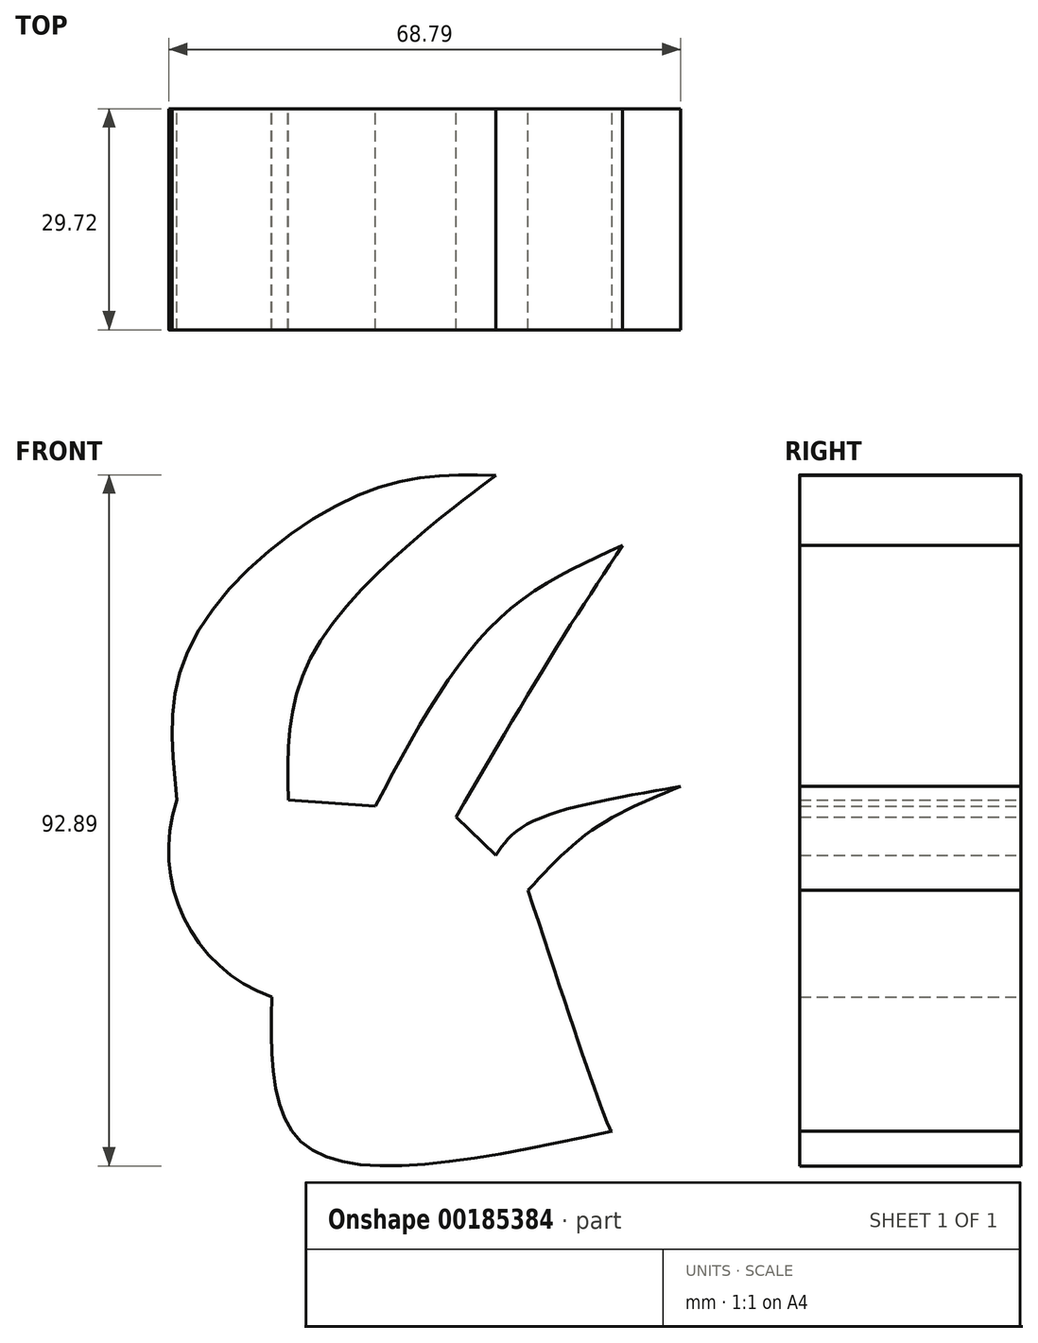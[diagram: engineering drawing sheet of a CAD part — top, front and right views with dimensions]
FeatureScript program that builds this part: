
annotation { "Feature Type Name" : "Feature", "Feature Type Description" : "" }
export const myFeature = defineFeature(function(context is Context, id is Id, definition is map)
    precondition{}
    {
        {
            var Q0;
            Q0=qCreatedBy(makeId("Front.planeOp"),FACE);
            var sketch = newSketch(context, id + "F0", { "sketchPlane" : qUnion([Q0])});
            skFitSpline(sketch, "E0", {"points": [v(-32.09, 23.68) * mm, v(-30.24, 44.6) * mm, v(-7.28, 64.9) * mm, v(10.76, 67.35) * mm], "startDerivative": vector(-7.35, 65.75) * mm, "endDerivative": vector(57.62, -1.36) * mm});
            skFitSpline(sketch, "E1", {"points": [v(-17.12, 23.68) * mm, v(-13.84, 43.36) * mm, v(4.61, 62.64) * mm, v(10.76, 67.35) * mm], "startDerivative": vector(-1.23, 54.75) * mm, "endDerivative": vector(22.37, 16.61) * mm});
            skFitSpline(sketch, "E2", {"points": [v(-5.43, 22.86) * mm, v(10.76, 47.67) * mm, v(27.78, 57.92) * mm], "startDerivative": vector(27.17, 51.27) * mm, "endDerivative": vector(39.68, 17.74) * mm});
            skFitSpline(sketch, "E3", {"points": [v(5.43, 21.43) * mm, v(18.76, 43.98) * mm, v(27.78, 57.92) * mm], "startDerivative": vector(24.94, 43.03) * mm, "endDerivative": vector(19.56, 29.45) * mm});
            skFitSpline(sketch, "E4", {"points": [v(35.57, 25.53) * mm, v(14.86, 20.4) * mm, v(10.76, 16.3) * mm], "startDerivative": vector(-37.93, -6.43) * mm, "endDerivative": vector(-8.62, -12.68) * mm});
            skFitSpline(sketch, "E5", {"points": [v(35.57, 25.53) * mm, v(23.89, 19.79) * mm, v(15.07, 11.58) * mm], "startDerivative": vector(-24.18, -9.87) * mm, "endDerivative": vector(-16.77, -18.07) * mm});
            skFitSpline(sketch, "E6", {"points": [v(-17.12, 23.68) * mm, v(-5.43, 22.86) * mm], "startDerivative": vector(11.69, -0.82) * mm, "endDerivative": vector(11.69, -0.82) * mm});
            skFitSpline(sketch, "E7", {"points": [v(5.43, 21.43) * mm, v(10.76, 16.3) * mm], "startDerivative": vector(5.33, -5.13) * mm, "endDerivative": vector(5.33, -5.13) * mm});
            skFitSpline(sketch, "E8", {"points": [v(15.07, 11.58) * mm, v(26.14, -20.6) * mm, v(26.35, -20.81) * mm], "startDerivative": vector(16.52, -50.14) * mm, "endDerivative": vector(2.02, -1.04) * mm});
            skArc(sketch, "E9", {"start": v(-32.09, 23.68) * mm, "mid": v(-31.16, 7.85) * mm, "end": v(-19.38, -2.77) * mm});
            skFitSpline(sketch, "E10", {"points": [v(-19.38, -2.77) * mm, v(-14.66, -22.86) * mm, v(26.35, -20.81) * mm], "startDerivative": vector(-0.81, -59.2) * mm, "endDerivative": vector(87.26, 18.7) * mm});
            skSolve(sketch);
        }
        {
            var Q0;
            Q0 = qSketchRegion(id + "F0", true);
            extrude(context, id + "F1", {"entities" : qUnion([Q0]), "depth" : 29.72 * mm});
        }
    });
